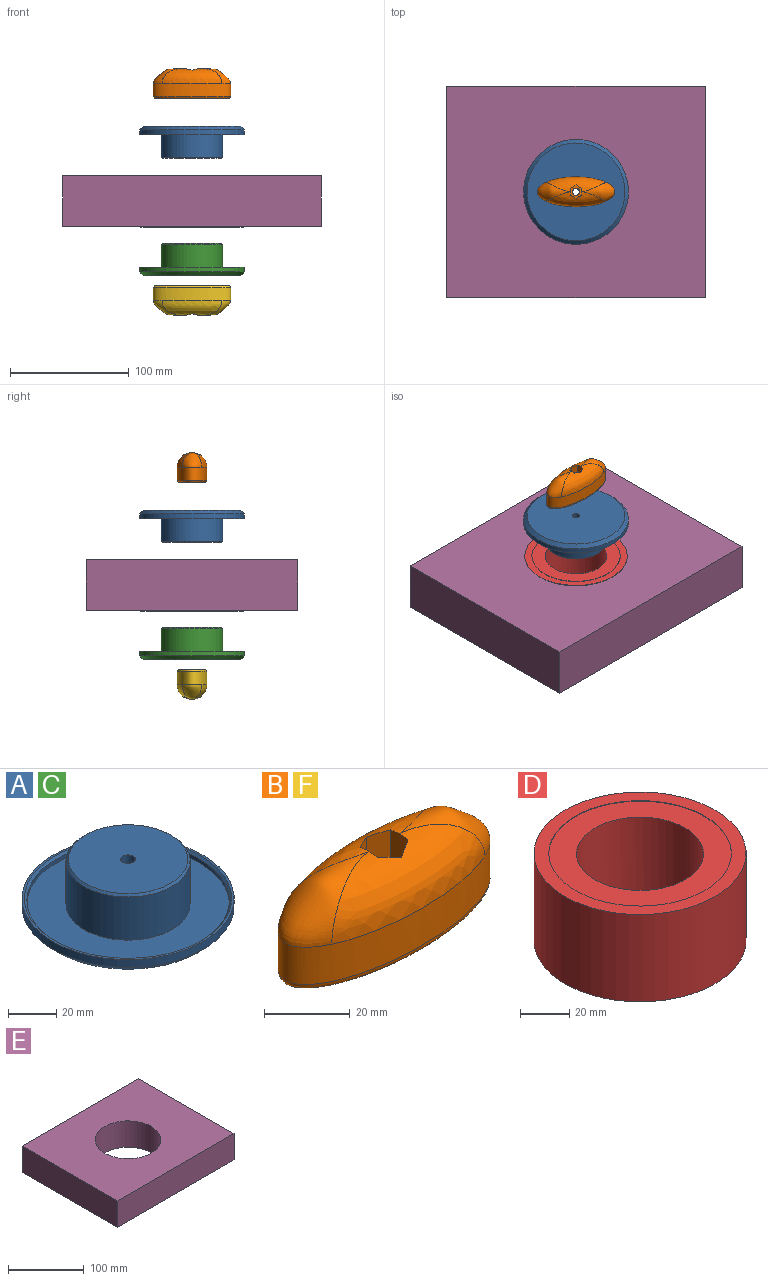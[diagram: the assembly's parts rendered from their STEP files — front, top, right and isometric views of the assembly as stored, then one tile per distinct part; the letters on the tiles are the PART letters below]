
ASSEMBLY  parts=6 mates=5
PART A: 11 faces, bbox 88.3x88.3x27 mm
  f0: cylinder r=44.17mm len=88.34mm, axis (0,0,-1), area 1110.1mm2, adj f1,f10
  f1: plane 88.34x88.34mm, normal (0,0,1), area 274.4mm2, adj f0,f8
  f2: plane 82.34x82.34mm, normal (0,0,-1), area 5295.7mm2, adj f7,f10
  f3: cylinder r=42.17mm len=84.34mm, axis (0,0,1), area 529.9mm2, adj f4,f8
  f4: plane 84.34x84.34mm, normal (0,0,1), area 3487.4mm2, adj f3,f5
  f5: cylinder r=25.85mm len=51.7mm, axis (0,0,-1), area 3573.2mm2, adj f4,f9
  f6: plane 49.7x49.7mm, normal (0,0,1), area 1910.8mm2, adj f7,f9
  f7: cylinder r=3.05mm len=27mm, axis (0,0,-1), area 517.4mm2, adj f2,f6
  f8: cone r=42.17mm half-angle=45deg, axis (0,0,1), area 379.2mm2, adj f1,f3
  f9: cone r=24.85mm half-angle=45deg, axis (0,0,-1), area 225.3mm2, adj f5,f6
  f10: cone r=44.17mm half-angle=45deg, axis (0,0,1), area 1137.5mm2, adj f0,f2
PART B: 17 faces, bbox 65.2x25.4x25.2 mm
  f0: plane 0.42x0.06mm, normal (0,0,1), area 0mm2, adj f4,f13,f14
  f1: plane 0.42x0.06mm, normal (0,0,1), area 0mm2, adj f7,f13,f14
  f2: extruded ~65.03x25.21mm, area 1577.1mm2, adj f12,f13,f14,f15,f16
  f3: plane 61.05x21.22mm, normal (0,0,-1), area 973.8mm2, adj f11,f16
  f4: plane 15.07x5.84mm, normal (-1,0,0), area 86mm2, adj f0,f5,f9,f10,f13,f14
  f5: plane 14.83x5.17mm, normal (-0.5,-0.87,0), area 82.2mm2, adj f4,f6,f10,f13
  f6: plane 14.82x5.15mm, normal (0.5,-0.87,0), area 82.2mm2, adj f5,f7,f10,f13
  f7: plane 15.07x5.84mm, normal (1,0,0), area 86mm2, adj f1,f6,f8,f10,f13,f14
  f8: plane 14.83x5.17mm, normal (0.5,0.87,0), area 82.2mm2, adj f7,f9,f10,f14
  f9: plane 14.82x5.15mm, normal (-0.5,0.87,0), area 82.2mm2, adj f4,f8,f10,f14
  f10: plane 11.55x10mm, normal (0,0,1), area 57.4mm2, adj f4,f5,f6,f7,f8,f9,f11
  f11: cylinder r=3.05mm len=10mm, axis (0,0,-1), area 191.6mm2, adj f3,f10
  f12: bspline ~27.1x15.98mm, area 257mm2, adj f2,f13,f14
  f13: bspline ~51.55x16.02mm, area 716.3mm2, adj f0,f1,f2,f4,f5,f6,f7,f12
  f14: bspline ~51.73x16.04mm, area 717.1mm2, adj f0,f1,f2,f4,f7,f8,f9,f12
  f15: bspline ~27.1x15.96mm, area 256.7mm2, adj f2,f13,f14
  f16: bspline ~65.05x25.23mm, area 453.5mm2, adj f2,f3
PART C: same geometry as A
PART D: 8 faces, bbox 86.3x86.3x43.5 mm
  f0: cylinder r=25.85mm len=51.7mm, axis (0,0,1), area 6984.1mm2, adj f5,f6
  f1: cylinder r=43.17mm len=86.34mm, axis (0,0,-1), area 11799.2mm2, adj f2,f3
  f2: plane 86.34x86.34mm, normal (0,0,1), area 1514.4mm2, adj f1,f4
  f3: plane 86.34x86.34mm, normal (0,0,-1), area 1514.4mm2, adj f1,f7
  f4: cylinder r=37.17mm len=74.34mm, axis (0,0,1), area 58.4mm2, adj f2,f5
  f5: plane 74.34x74.34mm, normal (0,0,1), area 2241.2mm2, adj f0,f4
  f6: plane 74.34x74.34mm, normal (0,0,-1), area 2241.2mm2, adj f0,f7
  f7: cylinder r=37.17mm len=74.34mm, axis (0,0,-1), area 58.4mm2, adj f3,f6
PART E: 7 faces, bbox 217.7x177.7x42.5 mm
  f0: plane 177.68x42.5mm, normal (1,0,0), area 7551.2mm2, adj f1,f3,f4,f5
  f1: plane 217.66x42.5mm, normal (0,1,0), area 9250.5mm2, adj f0,f2,f4,f5
  f2: plane 177.68x42.5mm, normal (-1,0,0), area 7551.2mm2, adj f1,f3,f4,f5
  f3: plane 217.66x42.5mm, normal (0,-1,0), area 9250.5mm2, adj f0,f2,f4,f5
  f4: plane 217.66x177.68mm, normal (0,0,1), area 32817.8mm2, adj f0,f1,f2,f3,f6
  f5: plane 217.66x177.68mm, normal (0,0,-1), area 32817.8mm2, adj f0,f1,f2,f3,f6
  f6: cylinder r=43.17mm len=86.34mm, axis (0,0,1), area 11527.9mm2, adj f4,f5
PART F: same geometry as B
PLACE A rot(axis=(1,0,0),180deg) t=(-6.74,1.61,67.42)mm
PLACE B t=(-6.74,1.61,90.88)mm
PLACE C t=(-6.74,1.61,-58.29)mm
PLACE D rot(axis=(0,0,-1),0deg) t=(-6.74,1.61,-17.41)mm
PLACE E t=(-6.74,1.61,-16.8)mm
PLACE F rot(axis=(1,0,0),180deg) t=(-6.74,1.61,-66.76)mm
MATE cylindrical D.f0 <-> C.f5  axis (0,0,1) through (-6.74,1.61,-17.16)mm
MATE cylindrical D.f1 <-> E.f6  axis (0,0,-1) through (-6.74,1.61,4.34)mm
MATE cylindrical A.f5 <-> D.f0  axis (0,0,1) through (-6.74,1.61,41.42)mm
MATE cylindrical A.f7 <-> B.f11  axis (0,0,1) through (-6.74,1.61,53.92)mm
MATE cylindrical C.f7 <-> F.f11  axis (0,0,-1) through (-6.74,1.61,-44.79)mm
